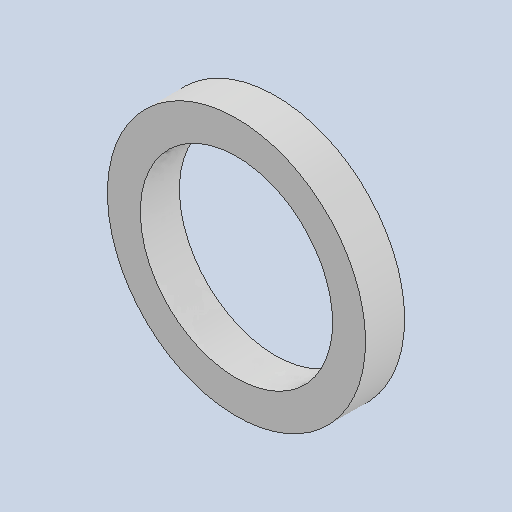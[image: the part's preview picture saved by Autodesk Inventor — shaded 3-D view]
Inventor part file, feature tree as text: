
AUTODESK INVENTOR PART (.ipt)
format: ipt  version: 2023 (Build 270158000, 158)  size: 138,240 bytes
history: native  units: in
note: dims shown in document units (in); Inventor stores cm internally (conversion verified against a paired STEP export)
features: extrude x1, sketch x1
ambient origin geometry x8: Origin, YZ Plane, XZ Plane, XY Plane, X Axis, Y Axis, Z Axis, Center Point
bodies: Solid1 (feature_tree)
feature tree (2):
  extrude  "Extrusion1"  Depth=0.28in
  sketch  "Sketch1"  dims[d0=1.378in d1=1.85in d2=0.28in d3=0.0in]
